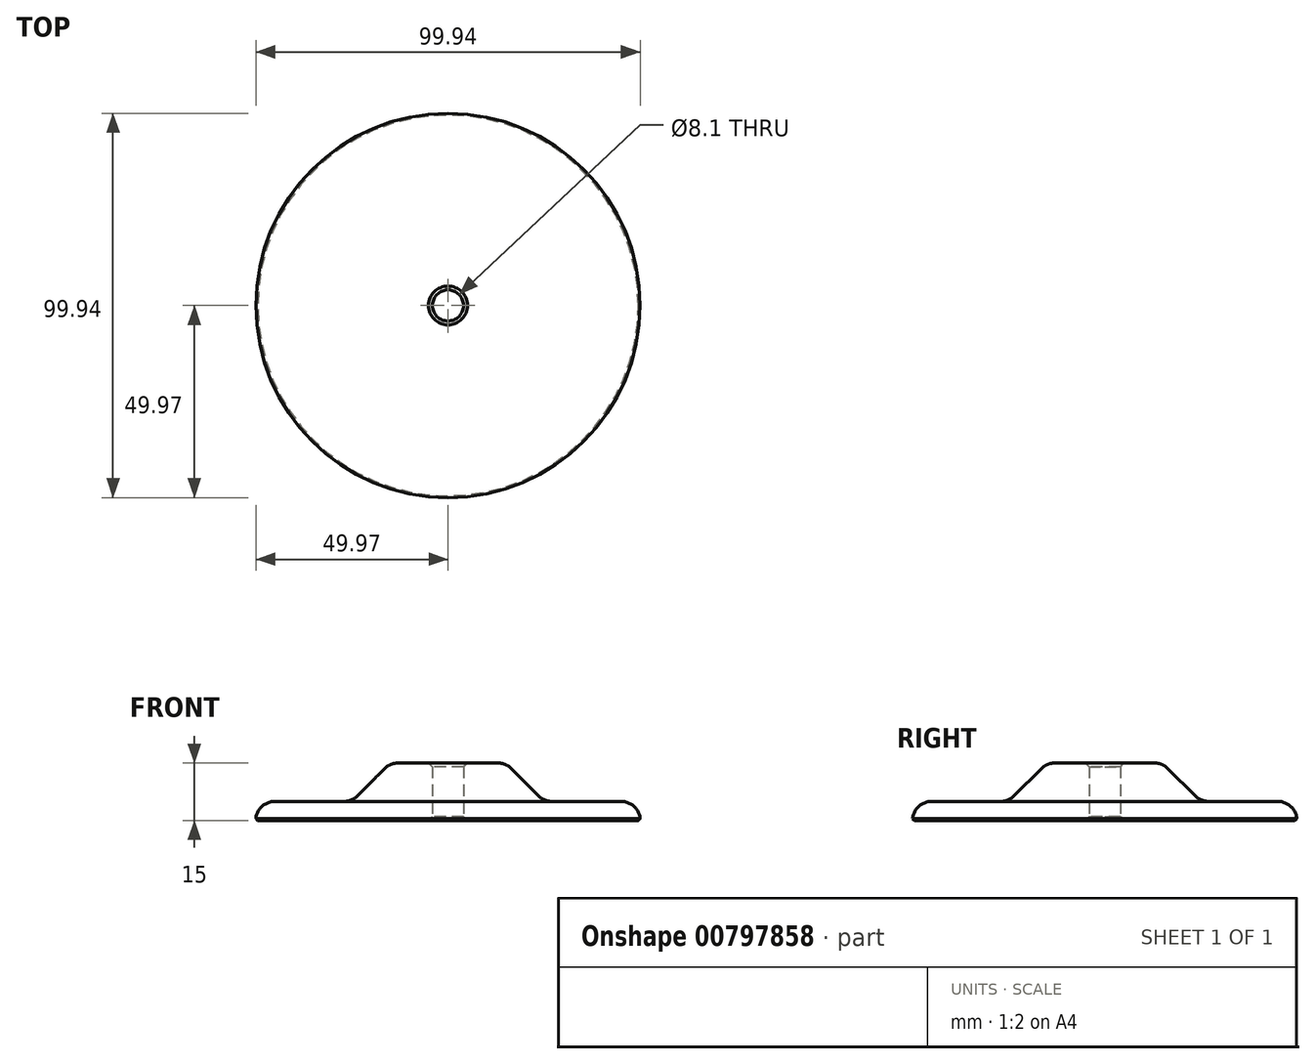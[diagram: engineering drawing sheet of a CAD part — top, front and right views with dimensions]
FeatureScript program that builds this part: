
annotation { "Feature Type Name" : "Feature", "Feature Type Description" : "" }
export const myFeature = defineFeature(function(context is Context, id is Id, definition is map)
    precondition{}
    {
        {
            var Q0;
            Q0=qCreatedBy(makeId("Top.planeOp"),FACE);
            var sketch = newSketch(context, id + "F0", { "sketchPlane" : qUnion([Q0])});
            skCircle(sketch, "E0", {"center": v(0, 0) * mm, "radius": 50 * mm});
            skCircle(sketch, "E1", {"center": v(0, 0) * mm, "radius": 4.05 * mm});
            skCircle(sketch, "E2", {"center": v(0, 0) * mm, "radius": 15 * mm});
            skSolve(sketch);
        }
        {
            var Q0;
            Q0=makeQuery(id+"F0.imprint","IMPRINT",FACE,{"disambiguationData":[TD([[makeQuery(id+"F0.imprint","IMPRINT",EDGE,{"derivedFrom":sQuery(id+"F0.wireOp",EDGE,"E0")}),1.0]])]});
            var Q1;
            Q1=makeQuery(id+"F0.imprint","IMPRINT",FACE,{"disambiguationData":[TD([[makeQuery(id+"F0.imprint","IMPRINT",EDGE,{"derivedFrom":sQuery(id+"F0.wireOp",EDGE,"E1")}),-1.0]])]});
            extrude(context, id + "F1", {"entities" : qUnion([Q0, Q1]), "depth" : 5 * mm, "offsetDistance" : 25 * mm});
        }
        {
            var Q0;
            Q0=makeQuery(id+"F0.imprint","IMPRINT",FACE,{"disambiguationData":[TD([[makeQuery(id+"F0.imprint","IMPRINT",EDGE,{"derivedFrom":sQuery(id+"F0.wireOp",EDGE,"E1")}),-1.0]])]});
            extrude(context, id + "F2", {"entities" : qUnion([Q0]), "operationType" : NewBodyOperationType.ADD, "depth" : 15 * mm, "offsetDistance" : 25 * mm});
        }
        {
            var Q0;
            Q0=makeQuery(id+"F2.boolean.opBoolean","INTERSECT",EDGE,{"derivedFrom":[makeQuery(id+"F1.opExtrude","CAP_FACE",FACE,{"disambiguationData":[OSD([sQuery(id+"F0.wireOp",EDGE,"E0"),sQuery(id+"F0.wireOp",EDGE,"E1")])],"isStart":false}),makeQuery(id+"F2.opExtrude","SWEPT_FACE",FACE,{"disambiguationData":[OSD([sQuery(id+"F0.wireOp",EDGE,"E2")])]})]});
            chamfer(context, id + "F3", {"entities" : qUnion([Q0]), "width" : 10 * mm, "tangentPropagation" : true});
        }
        {
            var Q0;
            {var subQ0=makeQuery(id+"F1.opExtrude","CAP_FACE",FACE,{"disambiguationData":[OSD([sQuery(id+"F0.wireOp",EDGE,"E0"),sQuery(id+"F0.wireOp",EDGE,"E1")])],"isStart":false});Q0=makeQuery(id+"F3.opChamfer","BLEND_EDGE",EDGE,{"blendedFrom":[makeQuery(id+"F2.boolean.opBoolean","INTERSECT",EDGE,{"derivedFrom":[subQ0,makeQuery(id+"F2.opExtrude","SWEPT_FACE",FACE,{"disambiguationData":[OSD([sQuery(id+"F0.wireOp",EDGE,"E2")])]})]}),subQ0],"blendedInto":[subQ0]});}
            var Q1;
            {var subQ0=sQuery(id+"F0.wireOp",EDGE,"E2");var subQ1=sQuery(id+"F0.wireOp",EDGE,"E1");Q1=makeQuery(id+"F3.opChamfer","BLEND_EDGE",EDGE,{"blendedFrom":[makeQuery(id+"F2.boolean.opBoolean","INTERSECT",EDGE,{"derivedFrom":[makeQuery(id+"F1.opExtrude","CAP_FACE",FACE,{"disambiguationData":[OSD([sQuery(id+"F0.wireOp",EDGE,"E0"),subQ1])],"isStart":false}),makeQuery(id+"F2.opExtrude","SWEPT_FACE",FACE,{"disambiguationData":[OSD([subQ0])]})]}),makeQuery(id+"F2.opExtrude","CAP_FACE",FACE,{"disambiguationData":[OSD([subQ1,subQ0])],"isStart":false})],"blendedInto":[makeQuery(id+"F2.opExtrude","CAP_FACE",FACE,{"disambiguationData":[OSD([subQ1,subQ0])],"isStart":false})]});}
            fillet(context, id + "F4", {"entities" : qUnion([Q0, Q1]), "radius" : 5 * mm, "tangentPropagation" : true, "allowEdgeOverflow" : false});
        }
        {
            var Q0;
            Q0=makeQuery(id+"F1.opExtrude","CAP_EDGE",EDGE,{"disambiguationData":[OSD([sQuery(id+"F0.wireOp",EDGE,"E0")])],"isStart":false});
            fillet(context, id + "F5", {"entities" : qUnion([Q0]), "radius" : 5 * mm, "tangentPropagation" : true, "allowEdgeOverflow" : false});
        }
        {
            var Q0;
            {var subQ0=sQuery(id+"F0.wireOp",EDGE,"E0");Q0=makeQuery(id+"F5.opFillet","BLEND_EDGE",EDGE,{"blendedFrom":[makeQuery(id+"F1.opExtrude","CAP_EDGE",EDGE,{"disambiguationData":[OSD([subQ0])],"isStart":false}),makeQuery(id+"F1.opExtrude","CAP_FACE",FACE,{"disambiguationData":[OSD([subQ0,sQuery(id+"F0.wireOp",EDGE,"E1")])],"isStart":true})],"blendedInto":[makeQuery(id+"F1.opExtrude","CAP_FACE",FACE,{"disambiguationData":[OSD([subQ0,sQuery(id+"F0.wireOp",EDGE,"E1")])],"isStart":true})]});}
            chamfer(context, id + "F6", {"entities" : qUnion([Q0]), "width" : 0.5 * mm, "tangentPropagation" : true});
        }
        {
            var Q0;
            Q0=makeQuery(id+"F2.opExtrude","CAP_EDGE",EDGE,{"disambiguationData":[OSD([sQuery(id+"F0.wireOp",EDGE,"E1")])],"isStart":false});
            var Q1;
            Q1=makeQuery(id+"F1.opExtrude","CAP_EDGE",EDGE,{"disambiguationData":[OSD([sQuery(id+"F0.wireOp",EDGE,"E1")])],"isStart":true});
            chamfer(context, id + "F7", {"entities" : qUnion([Q0, Q1]), "width" : 1 * mm, "tangentPropagation" : true});
        }
    });
